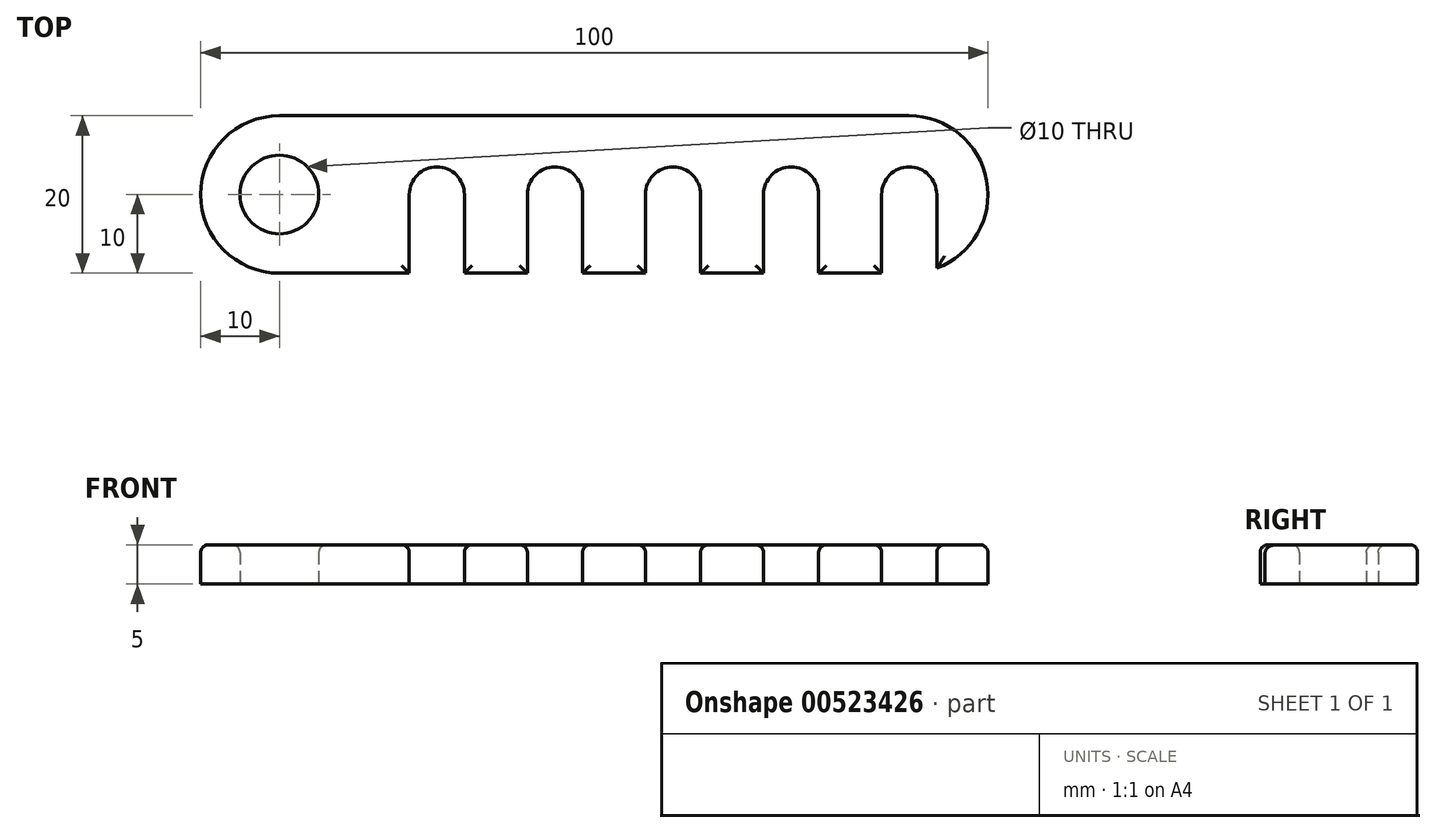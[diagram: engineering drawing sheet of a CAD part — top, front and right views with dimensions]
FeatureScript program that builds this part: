
annotation { "Feature Type Name" : "Feature", "Feature Type Description" : "" }
export const myFeature = defineFeature(function(context is Context, id is Id, definition is map)
    precondition{}
    {
        {
            var Q0;
            Q0=qCreatedBy(makeId("Top.planeOp"),FACE);
            var sketch = newSketch(context, id + "F0", { "sketchPlane" : qUnion([Q0])});
            skLineSegment(sketch, "E0.bottom", {"start": v(40, -10) * mm, "end": v(-40, -10) * mm});
            skLineSegment(sketch, "E0.top", {"start": v(40, 10) * mm, "end": v(-40, 10) * mm});
            skLineSegment(sketch, "E0.left", {"start": v(50, 0) * mm, "end": v(50, 0) * mm});
            skLineSegment(sketch, "E0.right", {"start": v(-50, 0) * mm, "end": v(-50, 0) * mm});
            skPoint(sketch, "E0.middle", {"position": v(0, 0) * mm});
            skPoint(sketch, "E1.visualSharp", {"position": v(-50, 10) * mm});
            skArc(sketch, "E1.filletArc", {"start": v(-40, 10) * mm, "mid": v(-47.07, 7.07) * mm, "end": v(-50, 0) * mm});
            skPoint(sketch, "E2.visualSharp", {"position": v(-50, -10) * mm});
            skArc(sketch, "E2.filletArc", {"start": v(-50, 0) * mm, "mid": v(-47.07, -7.07) * mm, "end": v(-40, -10) * mm});
            skPoint(sketch, "E3.visualSharp", {"position": v(50, -10) * mm});
            skArc(sketch, "E3.filletArc", {"start": v(40, -10) * mm, "mid": v(47.07, -7.07) * mm, "end": v(50, 0) * mm});
            skPoint(sketch, "E4.visualSharp", {"position": v(50, 10) * mm});
            skArc(sketch, "E4.filletArc", {"start": v(50, 0) * mm, "mid": v(47.07, 7.07) * mm, "end": v(40, 10) * mm});
            skCircle(sketch, "E5", {"center": v(-40, 0) * mm, "radius": 5 * mm});
            skCircle(sketch, "E6", {"center": v(40, 0) * mm, "radius": 3.5 * mm});
            skPoint(sketch, "E7", {"position": v(36.5, 0) * mm});
            skPoint(sketch, "E8", {"position": v(43.5, 0) * mm});
            skPoint(sketch, "E9", {"position": v(36.5, -10) * mm});
            skPoint(sketch, "E10", {"position": v(43.5, -10) * mm});
            skLineSegment(sketch, "E11.bottom", {"start": v(43.5, 0) * mm, "end": v(36.5, 0) * mm});
            skLineSegment(sketch, "E11.top", {"start": v(43.5, -10) * mm, "end": v(36.5, -10) * mm});
            skLineSegment(sketch, "E11.left", {"start": v(43.5, 0) * mm, "end": v(43.5, -10) * mm});
            skLineSegment(sketch, "E11.right", {"start": v(36.5, 0) * mm, "end": v(36.5, -10) * mm});
            skCircle(sketch, "E12.1.0.0", {"center": v(25, 0) * mm, "radius": 3.5 * mm});
            skLineSegment(sketch, "E12.1.0.1", {"start": v(21.5, 0) * mm, "end": v(21.5, -10) * mm});
            skLineSegment(sketch, "E12.1.0.2", {"start": v(28.5, 0) * mm, "end": v(28.5, -10) * mm});
            skLineSegment(sketch, "E12.1.0.3", {"start": v(28.5, -10) * mm, "end": v(21.5, -10) * mm});
            skCircle(sketch, "E12.2.0.0", {"center": v(10, 0) * mm, "radius": 3.5 * mm});
            skLineSegment(sketch, "E12.2.0.1", {"start": v(6.5, 0) * mm, "end": v(6.5, -10) * mm});
            skLineSegment(sketch, "E12.2.0.2", {"start": v(13.5, 0) * mm, "end": v(13.5, -10) * mm});
            skLineSegment(sketch, "E12.2.0.3", {"start": v(13.5, -10) * mm, "end": v(6.5, -10) * mm});
            skCircle(sketch, "E12.3.0.0", {"center": v(-5, 0) * mm, "radius": 3.5 * mm});
            skLineSegment(sketch, "E12.3.0.1", {"start": v(-8.5, 0) * mm, "end": v(-8.5, -10) * mm});
            skLineSegment(sketch, "E12.3.0.2", {"start": v(-1.5, 0) * mm, "end": v(-1.5, -10) * mm});
            skLineSegment(sketch, "E12.3.0.3", {"start": v(-1.5, -10) * mm, "end": v(-8.5, -10) * mm});
            skCircle(sketch, "E12.4.0.0", {"center": v(-20, 0) * mm, "radius": 3.5 * mm});
            skLineSegment(sketch, "E12.4.0.1", {"start": v(-23.5, 0) * mm, "end": v(-23.5, -10) * mm});
            skLineSegment(sketch, "E12.4.0.2", {"start": v(-16.5, 0) * mm, "end": v(-16.5, -10) * mm});
            skLineSegment(sketch, "E12.4.0.3", {"start": v(-16.5, -10) * mm, "end": v(-23.5, -10) * mm});
            skLineSegment(sketch, "E12.direction1", {"start": v(36.5, -10) * mm, "end": v(21.5, -10) * mm, "construction": true});
            skSolve(sketch);
        }
        {
            var Q0;
            Q0=makeQuery(id+"F0.imprint","IMPRINT",FACE,{"disambiguationData":[TD([[makeQuery(id+"F0.imprint","IMPRINT",EDGE,{"derivedFrom":sQuery(id+"F0.wireOp",EDGE,"E0.top")}),1.0]])]});
            extrude(context, id + "F1", {"entities" : qUnion([Q0]), "depth" : 5 * mm, "offsetDistance" : 25 * mm});
        }
        {
            var Q0;
            {var subQ0=sQuery(id+"F0.wireOp",EDGE,"E0.bottom");Q0=makeQuery(id+"F1.opExtrude","CAP_EDGE",EDGE,{"disambiguationData":[OSD([subQ0]),TDD([makeQuery(id+"F0.imprint","IMPRINT",EDGE,{"disambiguationData":[TD([[makeQuery(id+"F0.imprint","INTERSECT",VERTEX,{"derivedFrom":[subQ0,sQuery(id+"F0.wireOp",EDGE,"E2.filletArc")]}),1.0]])],"derivedFrom":subQ0})])],"isStart":false});}
            var Q1;
            Q1=makeQuery(id+"F1.opExtrude","CAP_EDGE",EDGE,{"disambiguationData":[OSD([sQuery(id+"F0.wireOp",EDGE,"E1.filletArc"),sQuery(id+"F0.wireOp",EDGE,"E2.filletArc")])],"isStart":false});
            var Q2;
            {var subQ0=sQuery(id+"F0.wireOp",EDGE,"E0.bottom");Q2=makeQuery(id+"F1.opExtrude","CAP_EDGE",EDGE,{"disambiguationData":[OSD([subQ0]),TDD([makeQuery(id+"F0.imprint","IMPRINT",EDGE,{"disambiguationData":[TD([[makeQuery(id+"F0.imprint","INTERSECT",VERTEX,{"derivedFrom":[subQ0,sQuery(id+"F0.wireOp",EDGE,"E12.3.0.1"),sQuery(id+"F0.wireOp",EDGE,"E12.3.0.3")]}),-1.0]])],"derivedFrom":subQ0})])],"isStart":false});}
            var Q3;
            {var subQ0=sQuery(id+"F0.wireOp",EDGE,"E0.bottom");Q3=makeQuery(id+"F1.opExtrude","CAP_EDGE",EDGE,{"disambiguationData":[OSD([subQ0]),TDD([makeQuery(id+"F0.imprint","IMPRINT",EDGE,{"disambiguationData":[TD([[makeQuery(id+"F0.imprint","INTERSECT",VERTEX,{"derivedFrom":[subQ0,sQuery(id+"F0.wireOp",EDGE,"E12.2.0.1"),sQuery(id+"F0.wireOp",EDGE,"E12.2.0.3")]}),-1.0]])],"derivedFrom":subQ0})])],"isStart":false});}
            var Q4;
            {var subQ0=sQuery(id+"F0.wireOp",EDGE,"E0.bottom");Q4=makeQuery(id+"F1.opExtrude","CAP_EDGE",EDGE,{"disambiguationData":[OSD([subQ0]),TDD([makeQuery(id+"F0.imprint","IMPRINT",EDGE,{"disambiguationData":[TD([[makeQuery(id+"F0.imprint","INTERSECT",VERTEX,{"derivedFrom":[subQ0,sQuery(id+"F0.wireOp",EDGE,"E12.1.0.1"),sQuery(id+"F0.wireOp",EDGE,"E12.1.0.3")]}),-1.0]])],"derivedFrom":subQ0})])],"isStart":false});}
            var Q5;
            {var subQ0=sQuery(id+"F0.wireOp",EDGE,"E0.bottom");Q5=makeQuery(id+"F1.opExtrude","CAP_EDGE",EDGE,{"disambiguationData":[OSD([subQ0]),TDD([makeQuery(id+"F0.imprint","IMPRINT",EDGE,{"disambiguationData":[TD([[makeQuery(id+"F0.imprint","INTERSECT",VERTEX,{"derivedFrom":[subQ0,sQuery(id+"F0.wireOp",EDGE,"E11.top"),sQuery(id+"F0.wireOp",EDGE,"E11.right")]}),-1.0]])],"derivedFrom":subQ0})])],"isStart":false});}
            var Q6;
            Q6=makeQuery(id+"F1.opExtrude","CAP_EDGE",EDGE,{"disambiguationData":[OSD([sQuery(id+"F0.wireOp",EDGE,"E3.filletArc"),sQuery(id+"F0.wireOp",EDGE,"E4.filletArc")])],"isStart":false});
            var Q7;
            Q7=makeQuery(id+"F1.opExtrude","CAP_EDGE",EDGE,{"disambiguationData":[OSD([sQuery(id+"F0.wireOp",EDGE,"E0.top")])],"isStart":false});
            var Q8;
            Q8=makeQuery(id+"F1.opExtrude","CAP_EDGE",EDGE,{"disambiguationData":[OSD([sQuery(id+"F0.wireOp",EDGE,"E5")])],"isStart":false});
            var Q9;
            Q9=makeQuery(id+"F1.opExtrude","CAP_EDGE",EDGE,{"disambiguationData":[OSD([sQuery(id+"F0.wireOp",EDGE,"E12.4.0.1")])],"isStart":false});
            var Q10;
            Q10=makeQuery(id+"F1.opExtrude","CAP_EDGE",EDGE,{"disambiguationData":[OSD([sQuery(id+"F0.wireOp",EDGE,"E12.4.0.0")])],"isStart":false});
            var Q11;
            Q11=makeQuery(id+"F1.opExtrude","CAP_EDGE",EDGE,{"disambiguationData":[OSD([sQuery(id+"F0.wireOp",EDGE,"E12.4.0.2")])],"isStart":false});
            var Q12;
            Q12=makeQuery(id+"F1.opExtrude","CAP_EDGE",EDGE,{"disambiguationData":[OSD([sQuery(id+"F0.wireOp",EDGE,"E12.3.0.1")])],"isStart":false});
            var Q13;
            Q13=makeQuery(id+"F1.opExtrude","CAP_EDGE",EDGE,{"disambiguationData":[OSD([sQuery(id+"F0.wireOp",EDGE,"E12.2.0.1")])],"isStart":false});
            var Q14;
            Q14=makeQuery(id+"F1.opExtrude","CAP_EDGE",EDGE,{"disambiguationData":[OSD([sQuery(id+"F0.wireOp",EDGE,"E12.1.0.1")])],"isStart":false});
            var Q15;
            Q15=makeQuery(id+"F1.opExtrude","CAP_EDGE",EDGE,{"disambiguationData":[OSD([sQuery(id+"F0.wireOp",EDGE,"E6")])],"isStart":false});
            fillet(context, id + "F2", {"entities" : qUnion([Q0, Q1, Q2, Q3, Q4, Q5, Q6, Q7, Q8, Q9, Q10, Q11, Q12, Q13, Q14, Q15]), "radius" : 1 * mm, "tangentPropagation" : true, "allowEdgeOverflow" : false});
        }
    });
